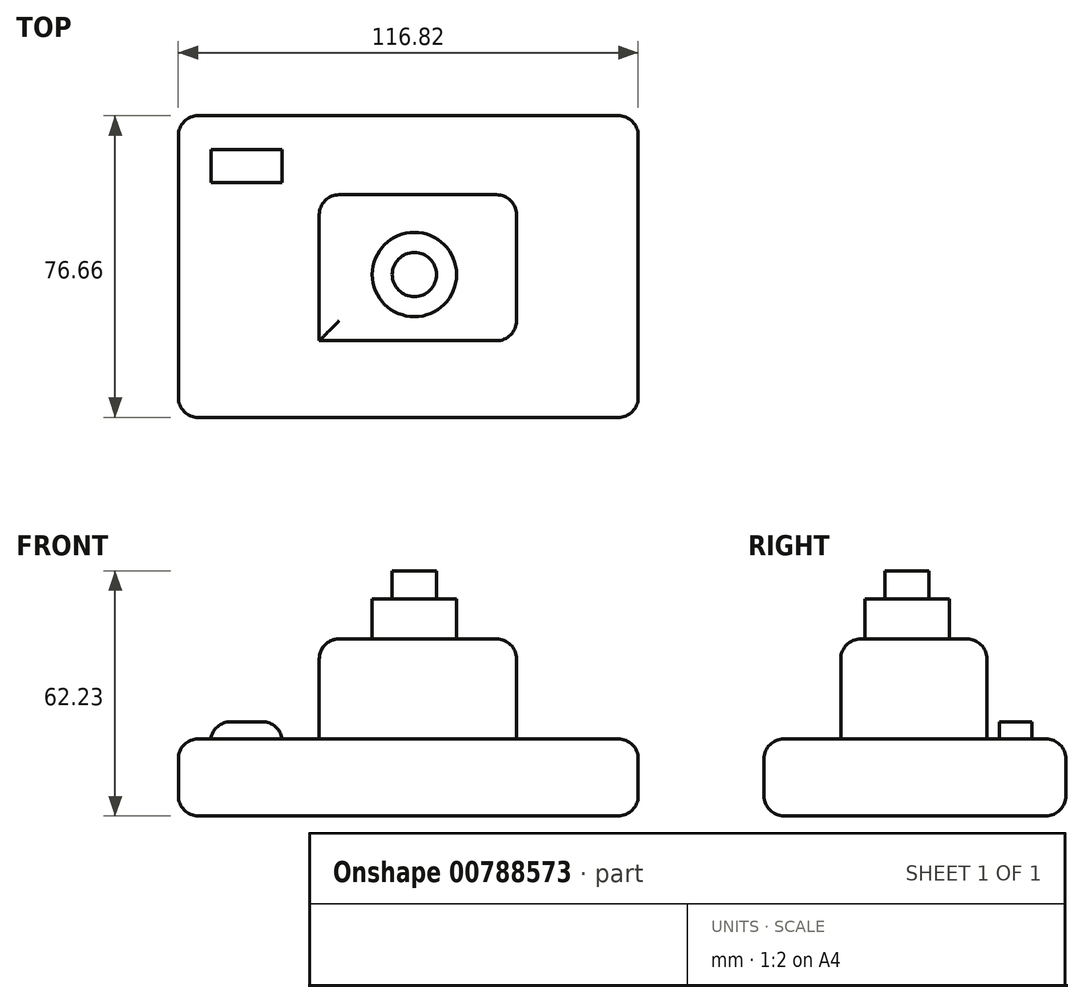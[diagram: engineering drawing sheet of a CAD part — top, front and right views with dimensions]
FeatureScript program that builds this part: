
annotation { "Feature Type Name" : "Feature", "Feature Type Description" : "" }
export const myFeature = defineFeature(function(context is Context, id is Id, definition is map)
    precondition{}
    {
        {
            var Q0;
            Q0=qCreatedBy(makeId("Top.planeOp"),FACE);
            var sketch = newSketch(context, id + "F0", { "sketchPlane" : qUnion([Q0])});
            skLineSegment(sketch, "E0.bottom", {"start": v(-59.96, 40.36) * mm, "end": v(56.86, 40.36) * mm});
            skLineSegment(sketch, "E0.top", {"start": v(-59.96, -36.3) * mm, "end": v(56.86, -36.3) * mm});
            skLineSegment(sketch, "E0.left", {"start": v(-59.96, 40.36) * mm, "end": v(-59.96, -36.3) * mm});
            skLineSegment(sketch, "E0.right", {"start": v(56.86, 40.36) * mm, "end": v(56.86, -36.3) * mm});
            skSolve(sketch);
        }
        {
            var Q0;
            Q0 = qSketchRegion(id + "F0", true);
            extrude(context, id + "F1", {"entities" : qUnion([Q0]), "depth" : 19.56 * mm, "offsetDistance" : 25.4 * mm});
        }
        {
            var Q0;
            Q0=makeQuery(id+"F1.opExtrude","CAP_EDGE",EDGE,{"disambiguationData":[OSD([sQuery(id+"F0.wireOp",EDGE,"E0.right")])],"isStart":false});
            var Q1;
            Q1=makeQuery(id+"F1.opExtrude","CAP_EDGE",EDGE,{"disambiguationData":[OSD([sQuery(id+"F0.wireOp",EDGE,"E0.bottom")])],"isStart":false});
            var Q2;
            Q2=makeQuery(id+"F1.opExtrude","CAP_EDGE",EDGE,{"disambiguationData":[OSD([sQuery(id+"F0.wireOp",EDGE,"E0.left")])],"isStart":false});
            var Q3;
            Q3=makeQuery(id+"F1.opExtrude","CAP_EDGE",EDGE,{"disambiguationData":[OSD([sQuery(id+"F0.wireOp",EDGE,"E0.top")])],"isStart":false});
            var Q4;
            Q4=makeQuery(id+"F1.opExtrude","CAP_EDGE",EDGE,{"disambiguationData":[OSD([sQuery(id+"F0.wireOp",EDGE,"E0.top")])],"isStart":true});
            var Q5;
            Q5=makeQuery(id+"F1.opExtrude","CAP_EDGE",EDGE,{"disambiguationData":[OSD([sQuery(id+"F0.wireOp",EDGE,"E0.right")])],"isStart":true});
            var Q6;
            Q6=makeQuery(id+"F1.opExtrude","CAP_EDGE",EDGE,{"disambiguationData":[OSD([sQuery(id+"F0.wireOp",EDGE,"E0.bottom")])],"isStart":true});
            var Q7;
            Q7=makeQuery(id+"F1.opExtrude","CAP_EDGE",EDGE,{"disambiguationData":[OSD([sQuery(id+"F0.wireOp",EDGE,"E0.left")])],"isStart":true});
            var Q8;
            Q8=makeQuery(id+"F1.opExtrude","SWEPT_EDGE",EDGE,{"disambiguationData":[OSD([sQuery(id+"F0.wireOp",EDGE,"E0.bottom"),sQuery(id+"F0.wireOp",EDGE,"E0.left")])]});
            var Q9;
            Q9=makeQuery(id+"F1.opExtrude","SWEPT_EDGE",EDGE,{"disambiguationData":[OSD([sQuery(id+"F0.wireOp",EDGE,"E0.top"),sQuery(id+"F0.wireOp",EDGE,"E0.left")])]});
            var Q10;
            Q10=makeQuery(id+"F1.opExtrude","SWEPT_EDGE",EDGE,{"disambiguationData":[OSD([sQuery(id+"F0.wireOp",EDGE,"E0.bottom"),sQuery(id+"F0.wireOp",EDGE,"E0.right")])]});
            var Q11;
            Q11=makeQuery(id+"F1.opExtrude","SWEPT_EDGE",EDGE,{"disambiguationData":[OSD([sQuery(id+"F0.wireOp",EDGE,"E0.top"),sQuery(id+"F0.wireOp",EDGE,"E0.right")])]});
            fillet(context, id + "F2", {"entities" : qUnion([Q0, Q1, Q2, Q3, Q4, Q5, Q6, Q7, Q8, Q9, Q10, Q11]), "radius" : 5.08 * mm, "tangentPropagation" : true, "allowEdgeOverflow" : false});
        }
        {
            var Q0;
            Q0=makeQuery(id+"F1.opExtrude","CAP_FACE",FACE,{"disambiguationData":[OSD([sQuery(id+"F0.wireOp",EDGE,"E0.bottom"),sQuery(id+"F0.wireOp",EDGE,"E0.top"),sQuery(id+"F0.wireOp",EDGE,"E0.left"),sQuery(id+"F0.wireOp",EDGE,"E0.right")])],"isStart":false});
            var sketch = newSketch(context, id + "F3", { "sketchPlane" : qUnion([Q0])});
            skLineSegment(sketch, "E1.bottom", {"start": v(-24.15, 20.27) * mm, "end": v(25.92, 20.27) * mm});
            skLineSegment(sketch, "E1.top", {"start": v(-24.15, -16.82) * mm, "end": v(25.92, -16.82) * mm});
            skLineSegment(sketch, "E1.left", {"start": v(-24.15, 20.27) * mm, "end": v(-24.15, -16.82) * mm});
            skLineSegment(sketch, "E1.right", {"start": v(25.92, 20.27) * mm, "end": v(25.92, -16.82) * mm});
            skSolve(sketch);
        }
        {
            var Q0;
            Q0 = qSketchRegion(id + "F3", true);
            extrude(context, id + "F4", {"entities" : qUnion([Q0]), "operationType" : NewBodyOperationType.ADD, "depth" : 25.4 * mm, "offsetDistance" : 25.4 * mm});
        }
        {
            var Q0;
            Q0=makeQuery(id+"F4.opExtrude","CAP_EDGE",EDGE,{"disambiguationData":[OSD([sQuery(id+"F3.wireOp",EDGE,"E1.top")])],"isStart":false});
            var Q1;
            Q1=makeQuery(id+"F4.opExtrude","CAP_EDGE",EDGE,{"disambiguationData":[OSD([sQuery(id+"F3.wireOp",EDGE,"E1.left")])],"isStart":false});
            var Q2;
            Q2=makeQuery(id+"F4.opExtrude","CAP_EDGE",EDGE,{"disambiguationData":[OSD([sQuery(id+"F3.wireOp",EDGE,"E1.bottom")])],"isStart":false});
            var Q3;
            Q3=makeQuery(id+"F4.opExtrude","CAP_EDGE",EDGE,{"disambiguationData":[OSD([sQuery(id+"F3.wireOp",EDGE,"E1.right")])],"isStart":false});
            var Q4;
            Q4=makeQuery(id+"F4.opExtrude","CAP_EDGE",EDGE,{"disambiguationData":[OSD([sQuery(id+"F3.wireOp",EDGE,"E1.right")])],"isStart":true});
            var Q5;
            Q5=makeQuery(id+"F4.opExtrude","SWEPT_EDGE",EDGE,{"disambiguationData":[OSD([sQuery(id+"F3.wireOp",EDGE,"E1.top"),sQuery(id+"F3.wireOp",EDGE,"E1.right")])]});
            var Q6;
            Q6=makeQuery(id+"F4.opExtrude","CAP_EDGE",EDGE,{"disambiguationData":[OSD([sQuery(id+"F3.wireOp",EDGE,"E1.left")])],"isStart":true});
            var Q7;
            Q7=makeQuery(id+"F4.opExtrude","CAP_EDGE",EDGE,{"disambiguationData":[OSD([sQuery(id+"F3.wireOp",EDGE,"E1.bottom")])],"isStart":true});
            var Q8;
            Q8=makeQuery(id+"F4.opExtrude","SWEPT_EDGE",EDGE,{"disambiguationData":[OSD([sQuery(id+"F3.wireOp",EDGE,"E1.bottom"),sQuery(id+"F3.wireOp",EDGE,"E1.right")])]});
            var Q9;
            Q9=makeQuery(id+"F4.opExtrude","SWEPT_EDGE",EDGE,{"disambiguationData":[OSD([sQuery(id+"F3.wireOp",EDGE,"E1.bottom"),sQuery(id+"F3.wireOp",EDGE,"E1.left")])]});
            fillet(context, id + "F5", {"entities" : qUnion([Q0, Q1, Q2, Q3, Q4, Q5, Q6, Q7, Q8, Q9]), "radius" : 5.08 * mm, "tangentPropagation" : true, "allowEdgeOverflow" : false});
        }
        {
            var Q0;
            Q0=makeQuery(id+"F1.opExtrude","CAP_FACE",FACE,{"disambiguationData":[OSD([sQuery(id+"F0.wireOp",EDGE,"E0.bottom"),sQuery(id+"F0.wireOp",EDGE,"E0.top"),sQuery(id+"F0.wireOp",EDGE,"E0.left"),sQuery(id+"F0.wireOp",EDGE,"E0.right")])],"isStart":false});
            var sketch = newSketch(context, id + "F6", { "sketchPlane" : qUnion([Q0])});
            skLineSegment(sketch, "E2.bottom", {"start": v(-51.7, 31.73) * mm, "end": v(-33.6, 31.73) * mm});
            skLineSegment(sketch, "E2.top", {"start": v(-51.7, 23.43) * mm, "end": v(-33.6, 23.43) * mm});
            skLineSegment(sketch, "E2.left", {"start": v(-51.7, 31.73) * mm, "end": v(-51.7, 23.43) * mm});
            skLineSegment(sketch, "E2.right", {"start": v(-33.6, 31.73) * mm, "end": v(-33.6, 23.43) * mm});
            skSolve(sketch);
        }
        {
            var Q0;
            Q0 = qSketchRegion(id + "F6", true);
            extrude(context, id + "F7", {"entities" : qUnion([Q0]), "operationType" : NewBodyOperationType.ADD, "depth" : 4.32 * mm, "offsetDistance" : 25.4 * mm});
        }
        {
            var Q0;
            Q0=makeQuery(id+"F7.opExtrude","CAP_EDGE",EDGE,{"disambiguationData":[OSD([sQuery(id+"F6.wireOp",EDGE,"E2.left")])],"isStart":false});
            var Q1;
            Q1=makeQuery(id+"F7.opExtrude","CAP_EDGE",EDGE,{"disambiguationData":[OSD([sQuery(id+"F6.wireOp",EDGE,"E2.right")])],"isStart":false});
            fillet(context, id + "F8", {"entities" : qUnion([Q0, Q1]), "radius" : 5.08 * mm, "tangentPropagation" : true, "allowEdgeOverflow" : false});
        }
        {
            var Q0;
            Q0=makeQuery(id+"F4.opExtrude","CAP_FACE",FACE,{"disambiguationData":[OSD([sQuery(id+"F3.wireOp",EDGE,"E1.bottom"),sQuery(id+"F3.wireOp",EDGE,"E1.top"),sQuery(id+"F3.wireOp",EDGE,"E1.left"),sQuery(id+"F3.wireOp",EDGE,"E1.right")])],"isStart":false});
            var sketch = newSketch(context, id + "F9", { "sketchPlane" : qUnion([Q0])});
            skCircle(sketch, "E3", {"center": v(0, 0) * mm, "radius": 10.7 * mm});
            skSolve(sketch);
        }
        {
            var Q0;
            Q0 = qSketchRegion(id + "F9", true);
            extrude(context, id + "F10", {"entities" : qUnion([Q0]), "operationType" : NewBodyOperationType.ADD, "depth" : 10.16 * mm, "offsetDistance" : 25.4 * mm});
        }
        {
            var Q0;
            Q0=makeQuery(id+"F10.opExtrude","CAP_FACE",FACE,{"disambiguationData":[OSD([sQuery(id+"F9.wireOp",EDGE,"E3")])],"isStart":false});
            var sketch = newSketch(context, id + "F11", { "sketchPlane" : qUnion([Q0])});
            skCircle(sketch, "E4", {"center": v(0, 0) * mm, "radius": 5.61 * mm});
            skSolve(sketch);
        }
        {
            var Q0;
            Q0 = qSketchRegion(id + "F11", true);
            extrude(context, id + "F12", {"entities" : qUnion([Q0]), "operationType" : NewBodyOperationType.ADD, "depth" : 7.11 * mm, "offsetDistance" : 25.4 * mm});
        }
    });
